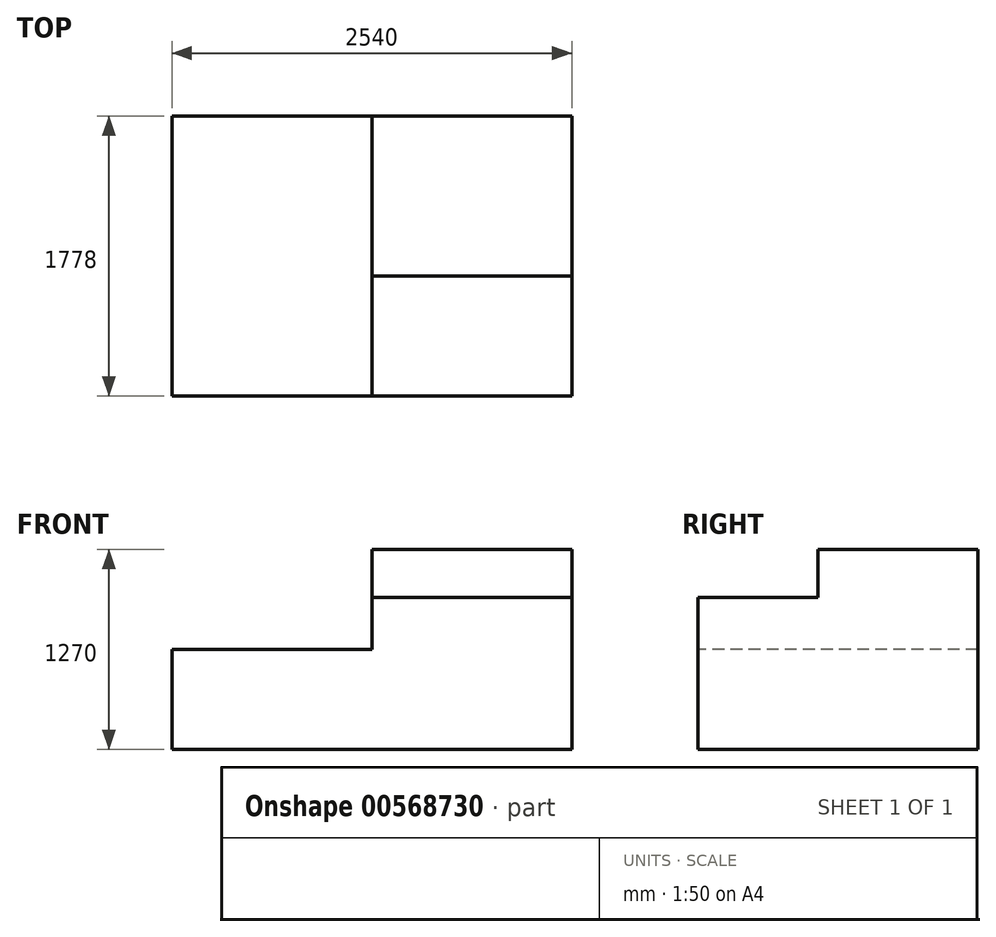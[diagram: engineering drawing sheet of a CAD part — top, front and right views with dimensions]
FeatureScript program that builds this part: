
annotation { "Feature Type Name" : "Feature", "Feature Type Description" : "" }
export const myFeature = defineFeature(function(context is Context, id is Id, definition is map)
    precondition{}
    {
        {
            var Q0;
            Q0=qCreatedBy(makeId("Right.planeOp"),FACE);
            var sketch = newSketch(context, id + "F0", { "sketchPlane" : qUnion([Q0])});
            skLineSegment(sketch, "E0", {"start": v(0, -76.27) * mm, "end": v(1778, -76.27) * mm});
            skLineSegment(sketch, "E1", {"start": v(1778, -76.27) * mm, "end": v(1778, 1193.73) * mm});
            skLineSegment(sketch, "E2", {"start": v(1778, 1193.73) * mm, "end": v(762, 1193.73) * mm});
            skLineSegment(sketch, "E3", {"start": v(762, 1193.73) * mm, "end": v(762, 888.93) * mm});
            skLineSegment(sketch, "E4", {"start": v(762, 888.93) * mm, "end": v(0, 888.93) * mm});
            skLineSegment(sketch, "E5", {"start": v(0, 888.93) * mm, "end": v(0, -76.27) * mm});
            skSolve(sketch);
        }
        {
            var Q0;
            Q0=makeQuery(id+"F0.imprint","IMPRINT",FACE,{"disambiguationData":[TD([[makeQuery(id+"F0.imprint","IMPRINT",EDGE,{"derivedFrom":sQuery(id+"F0.wireOp",EDGE,"E0")}),1.0]])]});
            extrude(context, id + "F1", {"entities" : qUnion([Q0]), "depth" : 1270 * mm, "offsetDistance" : 25.4 * mm});
        }
        {
            var Q0;
            Q0=makeQuery(id+"F1.opExtrude","SWEPT_FACE",FACE,{"disambiguationData":[OSD([sQuery(id+"F0.wireOp",EDGE,"E5")])]});
            var sketch = newSketch(context, id + "F2", { "sketchPlane" : qUnion([Q0])});
            skLineSegment(sketch, "E6", {"start": v(0, -76.27) * mm, "end": v(-1270, -76.27) * mm});
            skLineSegment(sketch, "E7", {"start": v(-1270, -76.27) * mm, "end": v(-1270, 558.73) * mm});
            skLineSegment(sketch, "E8", {"start": v(-1270, 558.73) * mm, "end": v(0, 558.73) * mm});
            skSolve(sketch);
        }
        {
            var Q0;
            Q0 = qSketchRegion(id + "F2", true);
            var Q1;
            {var subQ0=sQuery(id+"F2.wireOp",EDGE,"E6");Q1=makeQuery(id+"F2.imprint","IMPRINT",FACE,{"disambiguationData":[TD([[makeQuery(id+"F2.imprint","IMPRINT",EDGE,{"derivedFrom":subQ0}),-1.0]])]});}
            extrude(context, id + "F3", {"entities" : qUnion([Q0, Q1]), "operationType" : NewBodyOperationType.ADD, "oppositeDirection" : true, "depth" : 1778 * mm, "offsetDistance" : 25.4 * mm});
        }
    });
